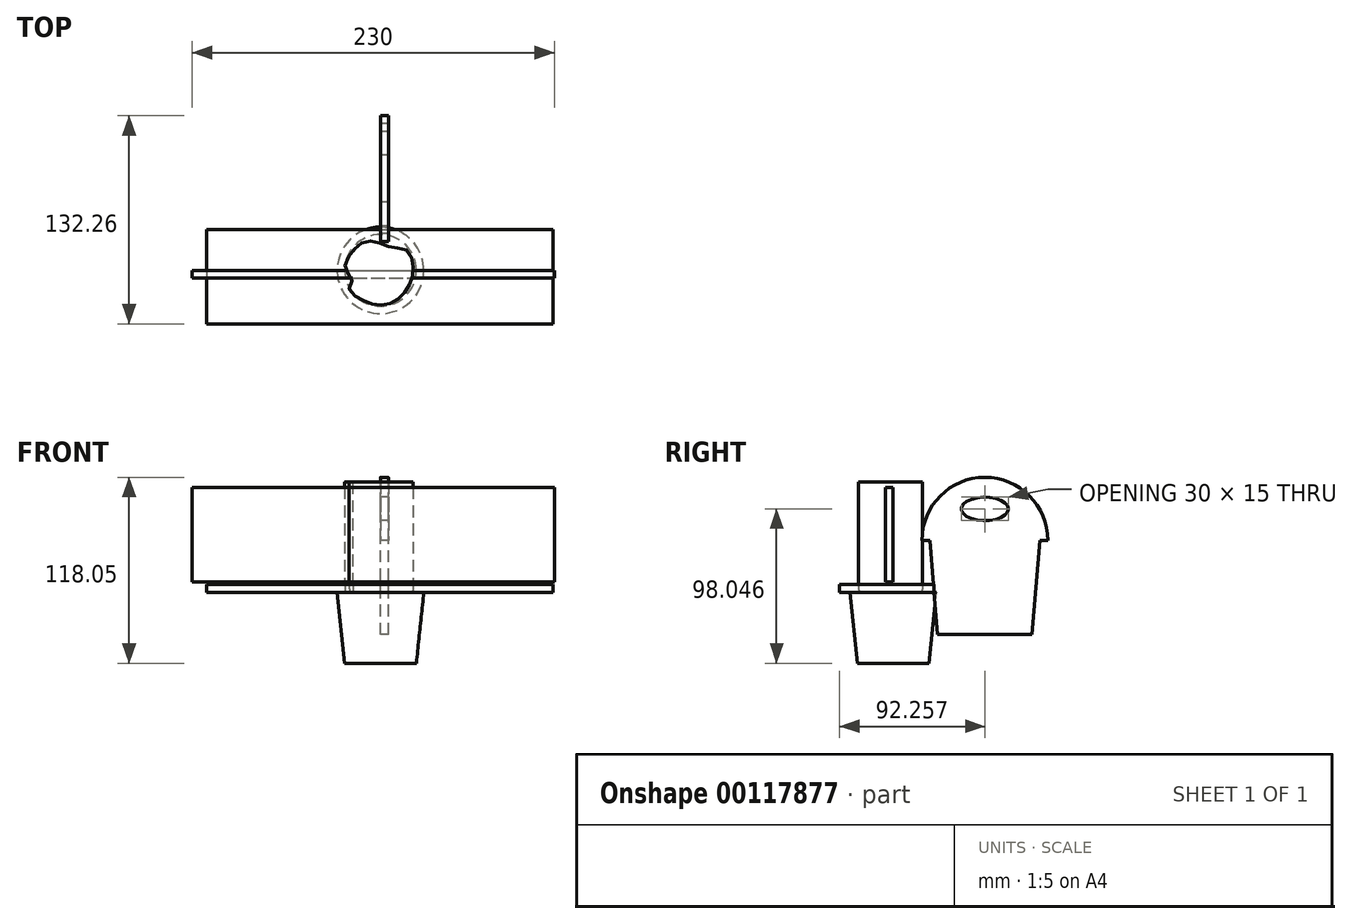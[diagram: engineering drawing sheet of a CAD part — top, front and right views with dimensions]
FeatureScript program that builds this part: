
annotation { "Feature Type Name" : "Feature", "Feature Type Description" : "" }
export const myFeature = defineFeature(function(context is Context, id is Id, definition is map)
    precondition{}
    {
        {
            var Q0;
            Q0=qCreatedBy(makeId("Top.planeOp"),FACE);
            var sketch = newSketch(context, id + "F0", { "sketchPlane" : qUnion([Q0])});
            skCircle(sketch, "E0", {"center": v(0, 0) * mm, "radius": 27.5 * mm});
            skSolve(sketch);
        }
        {
            var Q0;
            Q0 = qSketchRegion(id + "F0", true);
            extrude(context, id + "F1", {"entities" : qUnion([Q0]), "oppositeDirection" : true, "depth" : 45 * mm, "hasDraft" : true, "draftAngle" : 6 * degree, "draftPullDirection" : true});
        }
        {
            var Q0;
            Q0=makeQuery(id+"F1.opExtrude","CAP_FACE",FACE,{"disambiguationData":[OSD([sQuery(id+"F0.wireOp",EDGE,"E0")])],"isStart":true});
            var sketch = newSketch(context, id + "F2", { "sketchPlane" : qUnion([Q0])});
            skFitSpline(sketch, "E1", {"points": [v(-22, 0) * mm, v(-16.72, 12.76) * mm, v(-6.45, 18.33) * mm, v(7.04, 14.22) * mm, v(16.72, 12.47) * mm, v(19.94, -3.37) * mm, v(8.21, -19.8) * mm, v(-7.04, -20.38) * mm, v(-19.65, -11) * mm, v(-17.3, -4.55) * mm, v(-22, 0) * mm]});
            skSolve(sketch);
        }
        {
            var Q0;
            Q0 = qSketchRegion(id + "F2", true);
            var Q1;
            Q1=makeQuery(id+"F2.imprint","IMPRINT",FACE,{"disambiguationData":[TD([[makeQuery(id+"F2.imprint","IMPRINT",EDGE,{"derivedFrom":sQuery(id+"F2.wireOp",EDGE,"E1")}),-1.0]])]});
            extrude(context, id + "F3", {"entities" : qUnion([Q0, Q1]), "operationType" : NewBodyOperationType.ADD, "depth" : 5 * mm, "hasDraft" : true, "draftAngle" : 4 * degree});
        }
        {
            var Q0;
            Q0=makeQuery(id+"F3.opExtrude","CAP_FACE",FACE,{"disambiguationData":[OSD([sQuery(id+"F2.wireOp",EDGE,"E1")])],"isStart":false});
            extrude(context, id + "F4", {"entities" : qUnion([Q0]), "operationType" : NewBodyOperationType.ADD, "depth" : 65 * mm});
        }
        {
            var Q0;
            Q0=qCreatedBy(makeId("Top.planeOp"),FACE);
            var sketch = newSketch(context, id + "F5", { "sketchPlane" : qUnion([Q0])});
            skLineSegment(sketch, "E2.bottom", {"start": v(-110.45, 26) * mm, "end": v(109.55, 26) * mm});
            skLineSegment(sketch, "E2.top", {"start": v(-110.45, -34) * mm, "end": v(109.55, -34) * mm});
            skLineSegment(sketch, "E2.left", {"start": v(-110.45, 26) * mm, "end": v(-110.45, -34) * mm});
            skLineSegment(sketch, "E2.right", {"start": v(109.55, 26) * mm, "end": v(109.55, -34) * mm});
            skSolve(sketch);
        }
        {
            var Q0;
            Q0=makeQuery(id+"F5.imprint","IMPRINT",FACE,{"disambiguationData":[TD([[makeQuery(id+"F5.imprint","IMPRINT",EDGE,{"derivedFrom":sQuery(id+"F5.wireOp",EDGE,"E2.bottom")}),-1.0]])]});
            var Q1;
            Q1=sQuery(id+"F5.wireOp",EDGE,"E2.bottom");
            extrude(context, id + "F6", {"entities" : qUnion([Q0]), "surfaceEntities" : qUnion([Q1]), "depth" : 5 * mm});
        }
        {
            var Q0;
            Q0=qCreatedBy(makeId("Front.planeOp"),FACE);
            var sketch = newSketch(context, id + "F7", { "sketchPlane" : qUnion([Q0])});
            skLineSegment(sketch, "E3.bottom", {"start": v(-119.61, 66.7) * mm, "end": v(110.39, 66.7) * mm});
            skLineSegment(sketch, "E3.top", {"start": v(-119.61, 6.7) * mm, "end": v(110.39, 6.7) * mm});
            skLineSegment(sketch, "E3.left", {"start": v(-119.61, 66.7) * mm, "end": v(-119.61, 6.7) * mm});
            skLineSegment(sketch, "E3.right", {"start": v(110.39, 66.7) * mm, "end": v(110.39, 6.7) * mm});
            skSolve(sketch);
        }
        {
            var Q0;
            Q0 = qSketchRegion(id + "F7", true);
            extrude(context, id + "F8", {"entities" : qUnion([Q0]), "depth" : 5 * mm});
        }
        {
            var Q0;
            Q0=qCreatedBy(makeId("Right.planeOp"),FACE);
            var sketch = newSketch(context, id + "F9", { "sketchPlane" : qUnion([Q0])});
            skLineSegment(sketch, "E4.bottom", {"start": v(88.26, -26.75) * mm, "end": v(58.26, -26.75) * mm});
            skLineSegment(sketch, "E4.top", {"start": v(93.26, 33.05) * mm, "end": v(58.26, 33.05) * mm, "construction": true});
            skLineSegment(sketch, "E4.left", {"start": v(88.26, -26.75) * mm, "end": v(93.26, 33.05) * mm});
            skLineSegment(sketch, "E4.right", {"start": v(28.26, -26.75) * mm, "end": v(23.26, 33.05) * mm});
            skLineSegment(sketch, "E5", {"start": v(58.26, 33.05) * mm, "end": v(23.26, 33.05) * mm, "construction": true});
            skLineSegment(sketch, "E6", {"start": v(58.26, -26.75) * mm, "end": v(28.26, -26.75) * mm});
            skLineSegment(sketch, "E7", {"start": v(58.26, 33.05) * mm, "end": v(58.26, -26.75) * mm, "construction": true});
            skLineSegment(sketch, "E8", {"start": v(23.26, 33.05) * mm, "end": v(18.26, 33.05) * mm});
            skLineSegment(sketch, "E9", {"start": v(93.26, 33.05) * mm, "end": v(98.26, 33.05) * mm});
            skArc(sketch, "E10", {"start": v(18.26, 33.05) * mm, "mid": v(58.26, 73.05) * mm, "end": v(98.26, 33.05) * mm});
            skEllipse(sketch, "E11", {"center": v(58.26, 53.05) * mm, "majorRadius": 15 * mm, "minorRadius": 7.5 * mm, "majorAxis": v(1, 0)});
            skSolve(sketch);
        }
        {
            var Q0;
            Q0=makeQuery(id+"F9.imprint","IMPRINT",FACE,{"disambiguationData":[TD([[makeQuery(id+"F9.imprint","IMPRINT",EDGE,{"derivedFrom":sQuery(id+"F9.wireOp",EDGE,"E4.bottom")}),-1.0]])]});
            extrude(context, id + "F10", {"entities" : qUnion([Q0]), "depth" : 5 * mm});
        }
    });
